# Revit family: Faucet-Wall_Mount-Lavatory-KOHLER-Aleo-K-5684IN_1
name_source: partatom
category: Plumbing Fixtures
units: mm (PartAtom-declared; Revit-internal decimal feet)

## family parameters
Cut with Voids When Loaded = No
Host = Face
Maintain Annotation Orientation = No
OmniClass Number = 23.31.11.00
OmniClass Title = Faucets
Part Type = Normal
Room Calculation Point = No
Round Connector Dimension = Use Diameter
Shared = No

## types (5) — shared parameters
ADA Compliant = No
Assembly Code = D2010
CW Connection = Yes
Cold Water Inlet = Cold Water Inlet
Date Modified = 02/14/2022
Default Elevation = 36"
Description = Wall-mount Lavatory Faucet Trim In Polished Chrome
Drain Included = No
Flow Rate = 41 GPM
HW Connection = Yes
Handle Clearance = 3 7/8"
Height = 3 1/8"
Hot Water Inlet = Hot Water Inlet
Length = 6 5/16"
Manufacturer = KOHLER Co.
Master Format 2014 = 22 41 39
Master Format 2014 Name = Residential Faucets, Supplies, and Trim
Material = Premium Metal Construction
Pressure = 43.51 psi
Product Name = Aleo
Product Page URL = https://www.kohler.co.in
Spout Reach = 6 5/16"
URL = https://www.kohler.co.in
Vent Connection = No
Waste Connection = No
Waste Water Outlet = Waste Water Outlet
WaterSense Certified = No
Width = 7 7/8"

## per-type parameters (varying)
| type | Finish | Model | Type |
| AF-Vibrant French Gold | Kohler-Metal-AF-Vibrant_French_Gold | K-5684IN-4ND-AF | 1 |
| RGD-Polished Rose Gold | Kohler-Metal-RGD-Polished_Rose_Gold | K-5684IN-4ND-RGD | 2 |
| BN-Vibrant Brushed Nickel | Kohler-Metal-BN-Vibrant_Brushed_Nickel | K-5684IN-4ND-BN | 3 |
| CP-Polished Chrome | Kohler-Metal-CP-Polished_Chrome | K-5684IN-4ND-CP | 4 |
| BL-Matte Balck | Kohler-Metal-BL-Matte_Black | K-5684IN-4ND-BL | 5 |

## geometry (parser evidence)
native form markers: Sweep x6
no freeform markers — native parametric forms only
